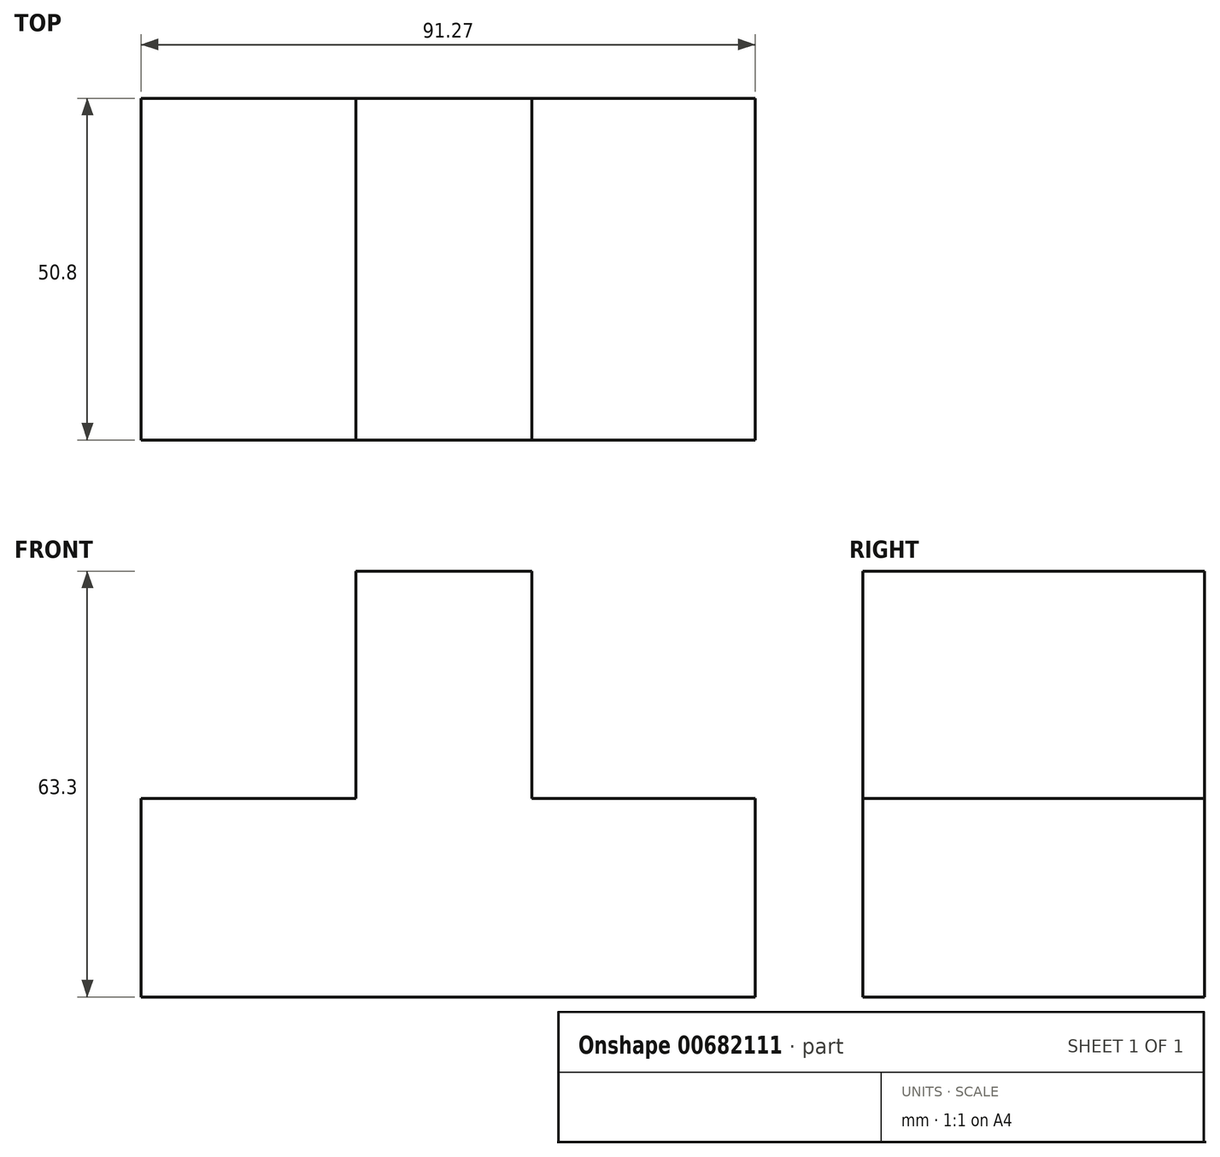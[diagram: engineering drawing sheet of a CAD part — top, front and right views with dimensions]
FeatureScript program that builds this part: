
annotation { "Feature Type Name" : "Feature", "Feature Type Description" : "" }
export const myFeature = defineFeature(function(context is Context, id is Id, definition is map)
    precondition{}
    {
        {
            var Q0;
            Q0=qCreatedBy(makeId("Front.planeOp"),FACE);
            var sketch = newSketch(context, id + "F0", { "sketchPlane" : qUnion([Q0])});
            skLineSegment(sketch, "E0", {"start": v(-47.64, 29.5) * mm, "end": v(-47.64, 0) * mm});
            skLineSegment(sketch, "E1", {"start": v(-47.64, 0) * mm, "end": v(43.63, 0) * mm});
            skLineSegment(sketch, "E2", {"start": v(43.63, 0) * mm, "end": v(43.63, 29.5) * mm});
            skLineSegment(sketch, "E3", {"start": v(-47.64, 29.5) * mm, "end": v(-15.75, 29.5) * mm});
            skLineSegment(sketch, "E4", {"start": v(-15.75, 29.5) * mm, "end": v(-15.75, 63.3) * mm});
            skLineSegment(sketch, "E5", {"start": v(-15.75, 63.3) * mm, "end": v(10.4, 63.3) * mm});
            skLineSegment(sketch, "E6", {"start": v(10.4, 63.3) * mm, "end": v(10.4, 29.5) * mm});
            skLineSegment(sketch, "E7", {"start": v(10.4, 29.5) * mm, "end": v(43.63, 29.5) * mm});
            skSolve(sketch);
        }
        {
            var Q0;
            Q0 = qSketchRegion(id + "F0", true);
            extrude(context, id + "F1", {"entities" : qUnion([Q0]), "depth" : 50.8 * mm, "offsetDistance" : 25.4 * mm});
        }
    });
